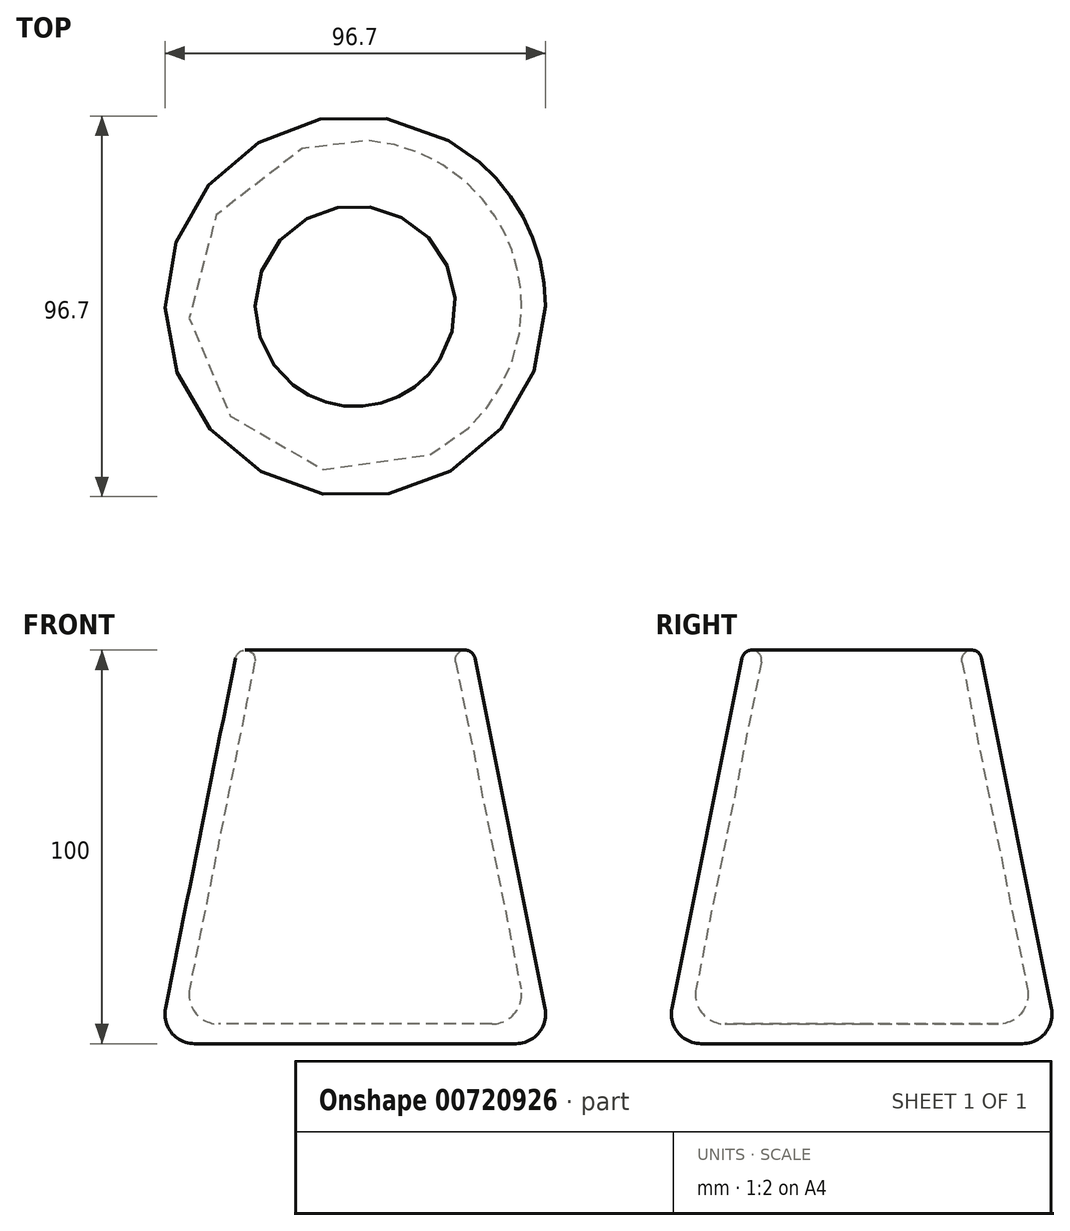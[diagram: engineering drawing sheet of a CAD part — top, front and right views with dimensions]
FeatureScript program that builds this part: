
annotation { "Feature Type Name" : "Feature", "Feature Type Description" : "" }
export const myFeature = defineFeature(function(context is Context, id is Id, definition is map)
    precondition{}
    {
        {
            var Q0;
            Q0=qCreatedBy(makeId("Top.planeOp"),FACE);
            var sketch = newSketch(context, id + "F0", { "sketchPlane" : qUnion([Q0])});
            skCircle(sketch, "E0", {"center": v(0, 0) * mm, "radius": 50 * mm});
            skSolve(sketch);
        }
        {
            var Q0;
            Q0=makeQuery(id+"F0.imprint","IMPRINT",FACE,{"disambiguationData":[TD([[makeQuery(id+"F0.imprint","IMPRINT",EDGE,{"derivedFrom":sQuery(id+"F0.wireOp",EDGE,"E0")}),1.0]])]});
            cPlane(context, id + "F1", {"entities" : qUnion([Q0]), "cplaneType" : CPlaneType.OFFSET, "offset" : 100 * mm, "width" : 150 * mm, "height" : 150 * mm});
        }
        {
            var Q0;
            Q0=qCreatedBy(id+"F1.planeOp",FACE);
            var sketch = newSketch(context, id + "F2", { "sketchPlane" : qUnion([Q0])});
            skCircle(sketch, "E1", {"center": v(0, 0) * mm, "radius": 30 * mm});
            skSolve(sketch);
        }
        {
            var Q0;
            Q0=makeQuery(id+"F0.imprint","IMPRINT",FACE,{"disambiguationData":[TD([[makeQuery(id+"F0.imprint","IMPRINT",EDGE,{"derivedFrom":sQuery(id+"F0.wireOp",EDGE,"E0")}),1.0]])]});
            var Q1;
            Q1=makeQuery(id+"F2.imprint","IMPRINT",FACE,{"disambiguationData":[TD([[makeQuery(id+"F2.imprint","IMPRINT",EDGE,{"derivedFrom":sQuery(id+"F2.wireOp",EDGE,"E1")}),1.0]])]});
            loft(context, id + "F3", {"sheetProfilesArray" : [{ "sheetProfileEntities" : qUnion([Q0]) }, { "sheetProfileEntities" : qUnion([Q1]) }]});
        }
        {
            var Q0;
            Q0=makeQuery(id+"F3.opLoft","CAP_FACE",FACE,{"disambiguationData":[OSD([makeQuery(id+"F2.imprint","IMPRINT",FACE,{"disambiguationData":[TD([[makeQuery(id+"F2.imprint","IMPRINT",EDGE,{"derivedFrom":sQuery(id+"F2.wireOp",EDGE,"E1")}),1.0]])]})])],"isStart":true});
            shell(context, id + "F4", {"entities" : qUnion([Q0]), "thickness" : 5 * mm});
        }
        {
            var Q0;
            Q0=makeQuery(id+"F3.opLoft","MID_CAP_EDGE",EDGE,{"disambiguationData":[OSD([sQuery(id+"F2.wireOp",EDGE,"E1")])],"capPos":1.0});
            var Q1;
            Q1=makeQuery(id+"F4.opShell","OFFSET_EDGE",EDGE,{"disambiguationData":[OSD([sQuery(id+"F2.wireOp",EDGE,"E1")])]});
            fillet(context, id + "F5", {"entities" : qUnion([Q0, Q1]), "radius" : 2.5 * mm, "tangentPropagation" : true, "allowEdgeOverflow" : false});
        }
        {
            var Q0;
            Q0=makeQuery(id+"F3.opLoft","MID_CAP_EDGE",EDGE,{"disambiguationData":[OSD([sQuery(id+"F0.wireOp",EDGE,"E0")])],"capPos":0.0});
            var Q1;
            Q1=makeQuery(id+"F4.opShell","OFFSET_EDGE",EDGE,{"disambiguationData":[OSD([sQuery(id+"F0.wireOp",EDGE,"E0")])]});
            fillet(context, id + "F6", {"entities" : qUnion([Q0, Q1]), "radius" : 7.5 * mm, "tangentPropagation" : true, "allowEdgeOverflow" : false});
        }
    });
